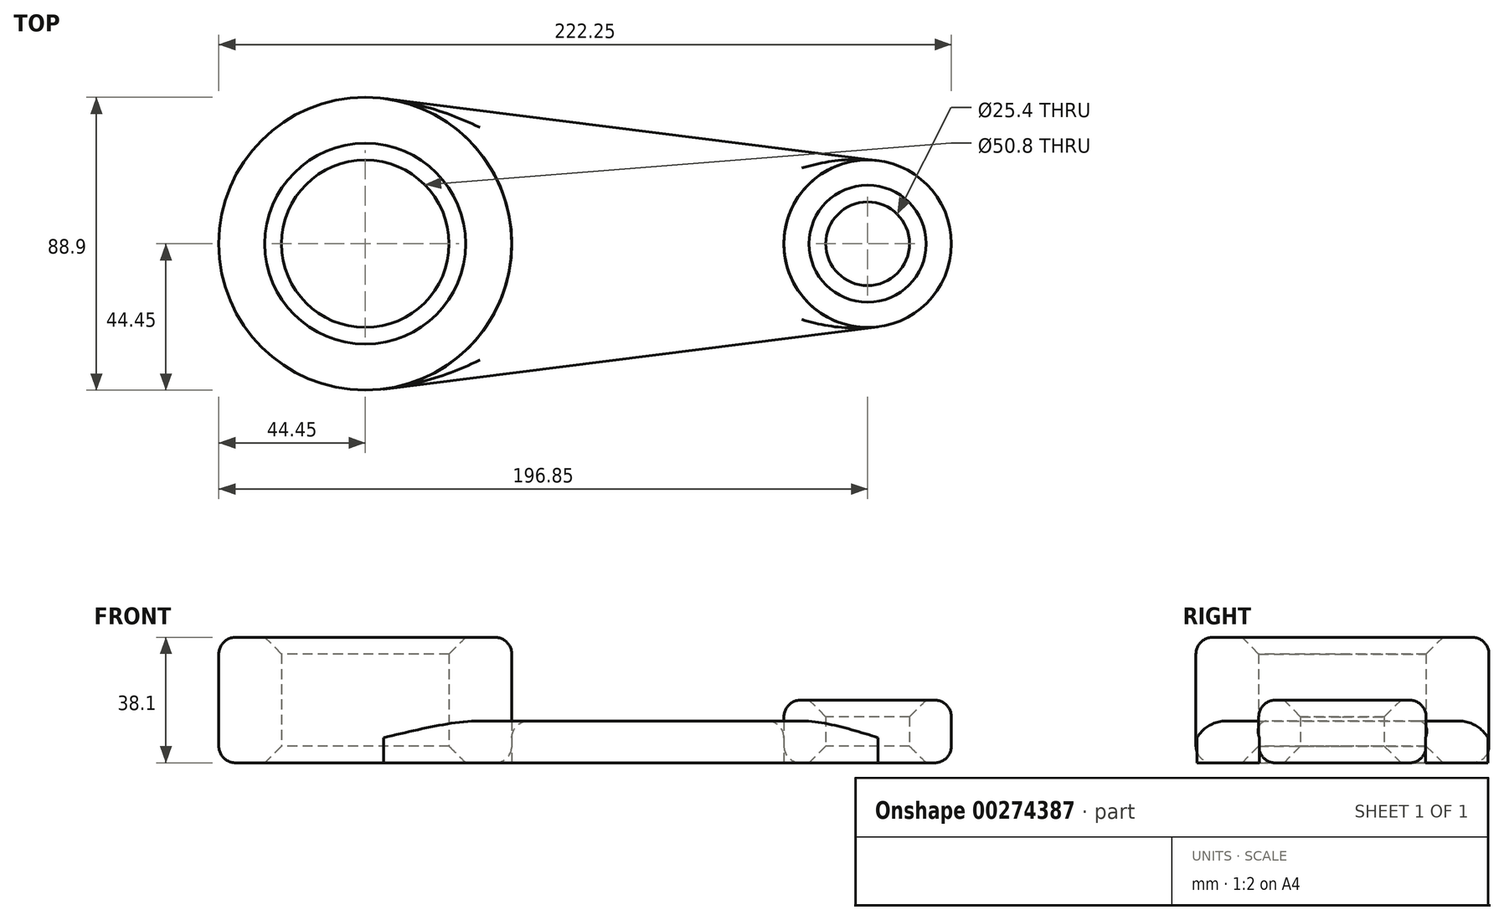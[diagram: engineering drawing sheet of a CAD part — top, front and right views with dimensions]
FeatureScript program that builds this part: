
annotation { "Feature Type Name" : "Feature", "Feature Type Description" : "" }
export const myFeature = defineFeature(function(context is Context, id is Id, definition is map)
    precondition{}
    {
        {
            var Q0;
            Q0=qCreatedBy(makeId("Top.planeOp"),FACE);
            var sketch = newSketch(context, id + "F0", { "sketchPlane" : qUnion([Q0])});
            skCircle(sketch, "E0", {"center": v(0, 0) * mm, "radius": 44.45 * mm});
            skCircle(sketch, "E1", {"center": v(0, 0) * mm, "radius": 25.4 * mm});
            skLineSegment(sketch, "E2", {"start": v(0, 0) * mm, "end": v(152.4, 0) * mm, "construction": true});
            skCircle(sketch, "E3", {"center": v(152.4, 0) * mm, "radius": 12.7 * mm});
            skCircle(sketch, "E4", {"center": v(152.4, 0) * mm, "radius": 25.4 * mm});
            skLineSegment(sketch, "E5", {"start": v(5.56, 44.1) * mm, "end": v(155.58, 25.2) * mm});
            skLineSegment(sketch, "E6", {"start": v(5.56, -44.1) * mm, "end": v(155.58, -25.2) * mm});
            skSolve(sketch);
        }
        {
            var Q0;
            Q0=makeQuery(id+"F0.imprint","IMPRINT",FACE,{"disambiguationData":[TD([[makeQuery(id+"F0.imprint","IMPRINT",EDGE,{"derivedFrom":sQuery(id+"F0.wireOp",EDGE,"E1")}),-1.0]])]});
            extrude(context, id + "F1", {"entities" : qUnion([Q0]), "depth" : 38.1 * mm});
        }
        {
            var Q0;
            Q0=makeQuery(id+"F0.imprint","IMPRINT",FACE,{"disambiguationData":[TD([[makeQuery(id+"F0.imprint","IMPRINT",EDGE,{"derivedFrom":sQuery(id+"F0.wireOp",EDGE,"E3")}),-1.0]])]});
            extrude(context, id + "F2", {"entities" : qUnion([Q0]), "depth" : 19.05 * mm});
        }
        {
            var Q0;
            {var subQ0=sQuery(id+"F0.wireOp",EDGE,"E5");Q0=makeQuery(id+"F0.imprint","IMPRINT",FACE,{"disambiguationData":[TD([[makeQuery(id+"F0.imprint","IMPRINT",EDGE,{"derivedFrom":subQ0}),-1.0]])]});}
            extrude(context, id + "F3", {"entities" : qUnion([Q0]), "depth" : 12.7 * mm});
        }
        {
            var Q0;
            Q0=makeQuery(id+"F3.opExtrude","CAP_FACE",FACE,{"disambiguationData":[OSD([sQuery(id+"F0.wireOp",EDGE,"E0"),sQuery(id+"F0.wireOp",EDGE,"E4"),sQuery(id+"F0.wireOp",EDGE,"E5"),sQuery(id+"F0.wireOp",EDGE,"E6")])],"isStart":false});
            fillet(context, id + "F4", {"entities" : qUnion([Q0]), "radius" : 5.08 * mm, "allowEdgeOverflow" : false});
        }
        {
            var Q0;
            Q0=makeQuery(id+"F1.opExtrude","SWEPT_FACE",FACE,{"disambiguationData":[OSD([sQuery(id+"F0.wireOp",EDGE,"E0")])]});
            fillet(context, id + "F5", {"entities" : qUnion([Q0]), "radius" : 5.08 * mm, "tangentPropagation" : true, "allowEdgeOverflow" : false});
        }
        {
            var Q0;
            Q0=makeQuery(id+"F1.opExtrude","SWEPT_FACE",FACE,{"disambiguationData":[OSD([sQuery(id+"F0.wireOp",EDGE,"E1")])]});
            chamfer(context, id + "F6", {"entities" : qUnion([Q0]), "width" : 5.08 * mm, "tangentPropagation" : true});
        }
        {
            var Q0;
            Q0=makeQuery(id+"F2.opExtrude","SWEPT_FACE",FACE,{"disambiguationData":[OSD([sQuery(id+"F0.wireOp",EDGE,"E4")])]});
            fillet(context, id + "F7", {"entities" : qUnion([Q0]), "radius" : 5.08 * mm, "tangentPropagation" : true, "allowEdgeOverflow" : false});
        }
        {
            var Q0;
            Q0=makeQuery(id+"F2.opExtrude","SWEPT_FACE",FACE,{"disambiguationData":[OSD([sQuery(id+"F0.wireOp",EDGE,"E3")])]});
            chamfer(context, id + "F8", {"entities" : qUnion([Q0]), "width" : 5.08 * mm, "tangentPropagation" : true});
        }
    });
